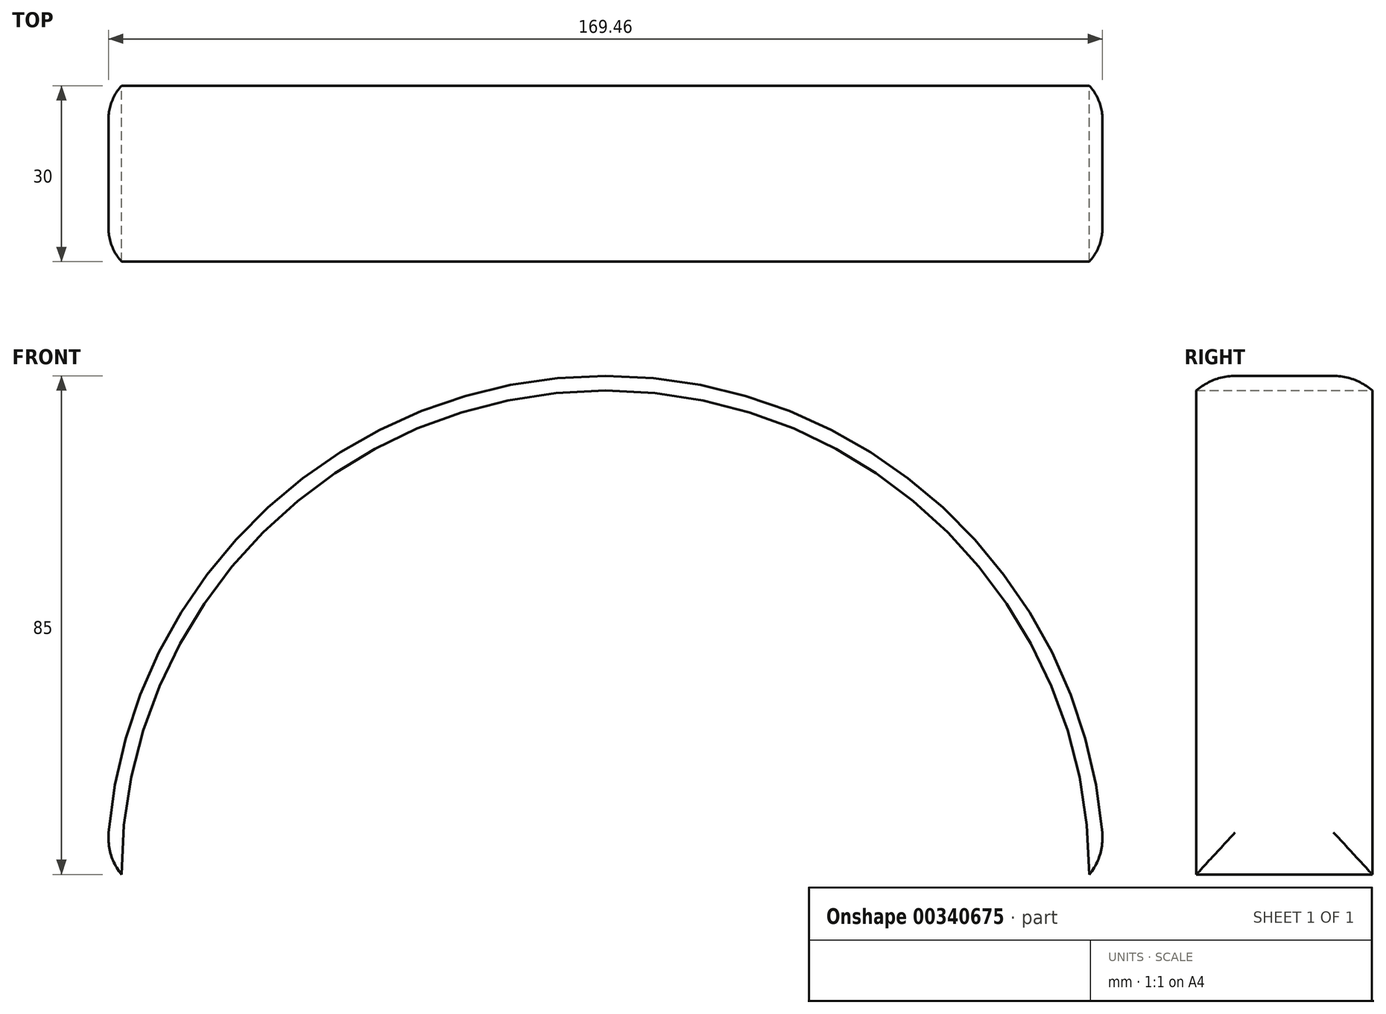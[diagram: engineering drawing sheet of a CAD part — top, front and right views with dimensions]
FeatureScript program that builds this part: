
annotation { "Feature Type Name" : "Feature", "Feature Type Description" : "" }
export const myFeature = defineFeature(function(context is Context, id is Id, definition is map)
    precondition{}
    {
        {
            var Q0;
            Q0=qCreatedBy(makeId("Front.planeOp"),FACE);
            var sketch = newSketch(context, id + "F0", { "sketchPlane" : qUnion([Q0])});
            skArc(sketch, "E0", {"start": v(-85, 0) * mm, "mid": v(0, 85) * mm, "end": v(85, 0) * mm});
            skArc(sketch, "E1", {"start": v(-82.5, 0) * mm, "mid": v(0, 82.5) * mm, "end": v(82.5, 0) * mm});
            skLineSegment(sketch, "E2", {"start": v(-82.5, 0) * mm, "end": v(-85, 0) * mm});
            skLineSegment(sketch, "E3", {"start": v(82.5, 0) * mm, "end": v(85, 0) * mm});
            skSolve(sketch);
        }
        {
            var Q0;
            Q0 = qSketchRegion(id + "F0", true);
            extrude(context, id + "F1", {"entities" : qUnion([Q0]), "depth" : 30 * mm});
        }
        {
            var Q0;
            Q0=makeQuery(id+"F1.opExtrude","SWEPT_FACE",FACE,{"disambiguationData":[OSD([sQuery(id+"F0.wireOp",EDGE,"E0")])]});
            fillet(context, id + "F2", {"entities" : qUnion([Q0]), "radius" : 10 * mm, "tangentPropagation" : true, "allowEdgeOverflow" : false});
        }
    });
